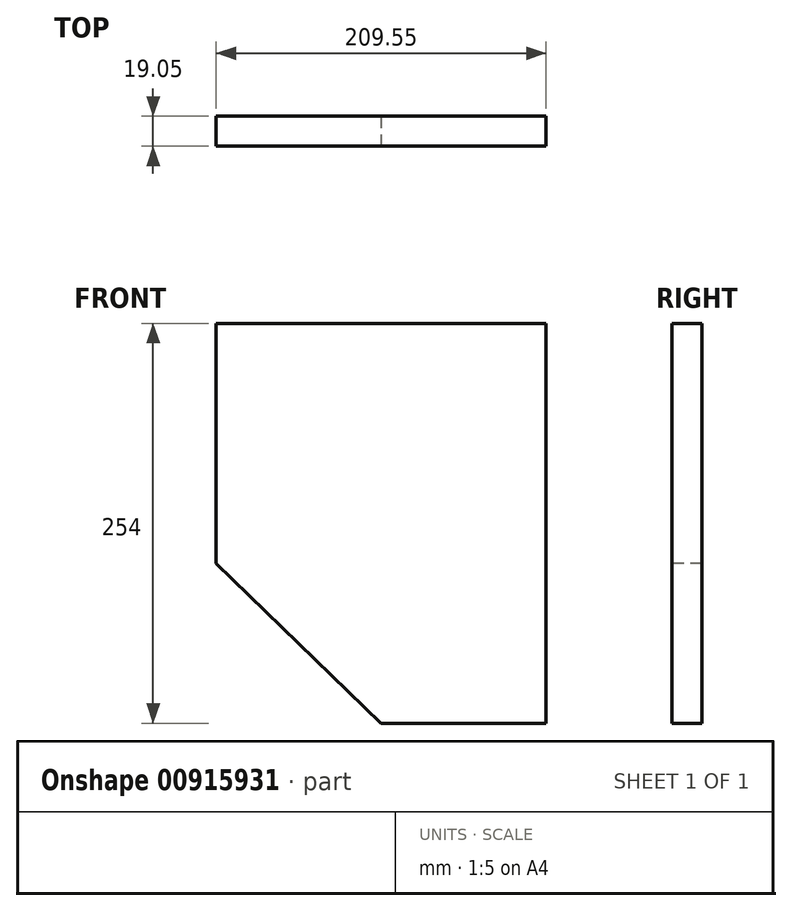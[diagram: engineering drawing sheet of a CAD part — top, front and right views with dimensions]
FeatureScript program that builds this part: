
annotation { "Feature Type Name" : "Feature", "Feature Type Description" : "" }
export const myFeature = defineFeature(function(context is Context, id is Id, definition is map)
    precondition{}
    {
        {
            var Q0;
            Q0=qCreatedBy(makeId("Front.planeOp"),FACE);
            var sketch = newSketch(context, id + "F0", { "sketchPlane" : qUnion([Q0])});
            skLineSegment(sketch, "E0.bottom", {"start": v(0, 0) * mm, "end": v(209.55, 0) * mm});
            skLineSegment(sketch, "E0.top", {"start": v(0, 254) * mm, "end": v(209.55, 254) * mm});
            skLineSegment(sketch, "E0.left", {"start": v(0, 0) * mm, "end": v(0, 254) * mm});
            skLineSegment(sketch, "E0.right", {"start": v(209.55, 0) * mm, "end": v(209.55, 254) * mm});
            skSolve(sketch);
        }
        {
            var Q0;
            Q0=qSketchRegion(id+"F0",true);
            extrude(context, id + "F1", {"entities" : qUnion([Q0]), "depth" : 19.05 * mm, "offsetDistance" : 25.4 * mm});
        }
        {
            var Q0;
            Q0=makeQuery(id+"F1.opExtrude","CAP_FACE",FACE,{"disambiguationData":[OSD([sQuery(id+"F0.wireOp",EDGE,"E0.bottom"),sQuery(id+"F0.wireOp",EDGE,"E0.top"),sQuery(id+"F0.wireOp",EDGE,"E0.left"),sQuery(id+"F0.wireOp",EDGE,"E0.right")])],"isStart":false});
            var sketch = newSketch(context, id + "F2", { "sketchPlane" : qUnion([Q0])});
            skLineSegment(sketch, "E1", {"start": v(104.78, 0) * mm, "end": v(0, 0) * mm});
            skLineSegment(sketch, "E2", {"start": v(0, 254) * mm, "end": v(0, 101.6) * mm, "construction": true});
            skLineSegment(sketch, "E3", {"start": v(0, 101.6) * mm, "end": v(104.78, 0) * mm});
            skLineSegment(sketch, "E4", {"start": v(0, 101.6) * mm, "end": v(0, 0) * mm});
            skSolve(sketch);
        }
        {
            var Q0;
            Q0=qSketchRegion(id+"F2",true);
            extrude(context, id + "F3", {"entities" : qUnion([Q0]), "operationType" : NewBodyOperationType.REMOVE, "endBound" : BoundingType.THROUGH_ALL, "oppositeDirection" : true, "depth" : 25.4 * mm, "offsetDistance" : 25.4 * mm});
        }
    });
